# Revit family: BalizadorConcreto_PBC10W-P_PBC10W-G_PowerLume
name_source: partatom
category: Luminárias
units: mm (PartAtom-declared; Revit-internal decimal feet)

## family parameters
Compartilhado = Sim
Corte com vazios quando carregada = Sim
Cota do conector redondo = Utilizar diâmetro
Fonte luminosa = Não
Hospedeiro = Face
Manter orientação da anotação = Não
Número OmniClass = 23.80.70.14.11.14
Ponto de cálculo do ambiente = Não
Tipo de parte = Normal
Título OmniClass = Post-Top Lighting

## types (2) — shared parameters
Carga Aparente Luminária = 0 VA
Catálogo de produtos = https://www.powerlume.com.br
Comentários de voltagem = 110 ou 220Vac 50/60Hz com driver incorporado
Contato do fabricante = (54) 3066-6488
Data da atualização = 06/03/2025
Descrição = Poste balizador LED em concreto
Difusor = PMMA transparente anti UV
Elevação-padrão = 1219 mm
Fabricante = Power Lume
Fator de Potência Luminária = 1
Fluxo luminoso = 858 lm
Frame = Concreto, leve
IP = 65
IRC = 90
IfcExportAs = IfcLightFixtureType
Largura = 150 mm
Localização = Caxias do Sul - RS / Brasil
Lâmpada = Placa LED
Peso = 0
Potência = 10W
Profundidade = 158 mm
Temperatura de cor = 3000K
Tipo de imagem = pbc10w.1237.png
URL = https://www.powerlume.com.br
URL do produto = https://www.powerlume.com.br
Versão = 1
Vida útil = 60000h
Voltagem Luminária = 0 V

## per-type parameters (varying)
| type | Altura | Modelo de luminária | Ângulo de abertura |
| PBC10W-G | 700 mm  [stored 2.29659 ft] | BalizadorConcreto_PBC10W-G_Base_PowerLume : PBC10W-G | Difuso assimétrico |
| PBC10W-P | 450 mm | BalizadorConcreto_PBC10W-P_Base_PowerLume : PBC10W-P | Difuso |

note: column(s) folded — value = type name in every type: Modelo

note: [stored X ft] marks values corroborated as IEEE doubles in the binary element streams (Revit-internal decimal feet)
